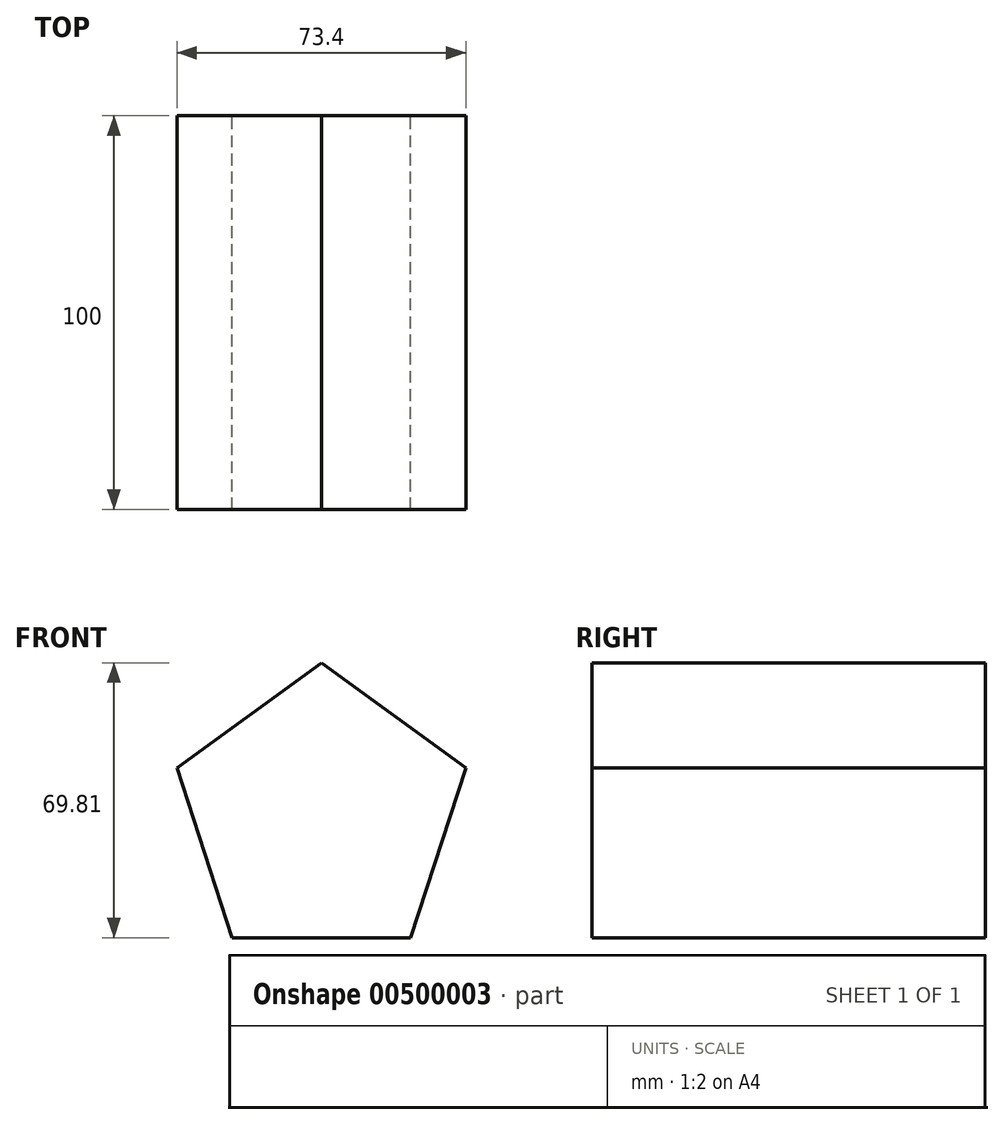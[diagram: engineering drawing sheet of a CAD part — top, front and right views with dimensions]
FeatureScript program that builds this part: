
annotation { "Feature Type Name" : "Feature", "Feature Type Description" : "" }
export const myFeature = defineFeature(function(context is Context, id is Id, definition is map)
    precondition{}
    {
        {
            var Q0;
            Q0=qCreatedBy(makeId("Front.planeOp"),FACE);
            var sketch = newSketch(context, id + "F0", { "sketchPlane" : qUnion([Q0])});
            skCircle(sketch, "E0.cCircle", {"center": v(0, 0) * mm, "radius": 38.59 * mm, "construction": true});
            skLineSegment(sketch, "E0.0", {"start": v(-36.7, 11.92) * mm, "end": v(0, 38.59) * mm});
            skLineSegment(sketch, "E0.1", {"start": v(0, 38.59) * mm, "end": v(36.7, 11.92) * mm});
            skLineSegment(sketch, "E0.2", {"start": v(36.7, 11.92) * mm, "end": v(22.68, -31.22) * mm});
            skLineSegment(sketch, "E0.3", {"start": v(22.68, -31.22) * mm, "end": v(-22.68, -31.22) * mm});
            skLineSegment(sketch, "E0.4", {"start": v(-22.68, -31.22) * mm, "end": v(-36.7, 11.92) * mm});
            skSolve(sketch);
        }
        {
            var Q0;
            Q0 = qSketchRegion(id + "F0", true);
            extrude(context, id + "F1", {"entities" : qUnion([Q0]), "endBound" : BoundingType.SYMMETRIC, "depth" : 100 * mm});
        }
    });
